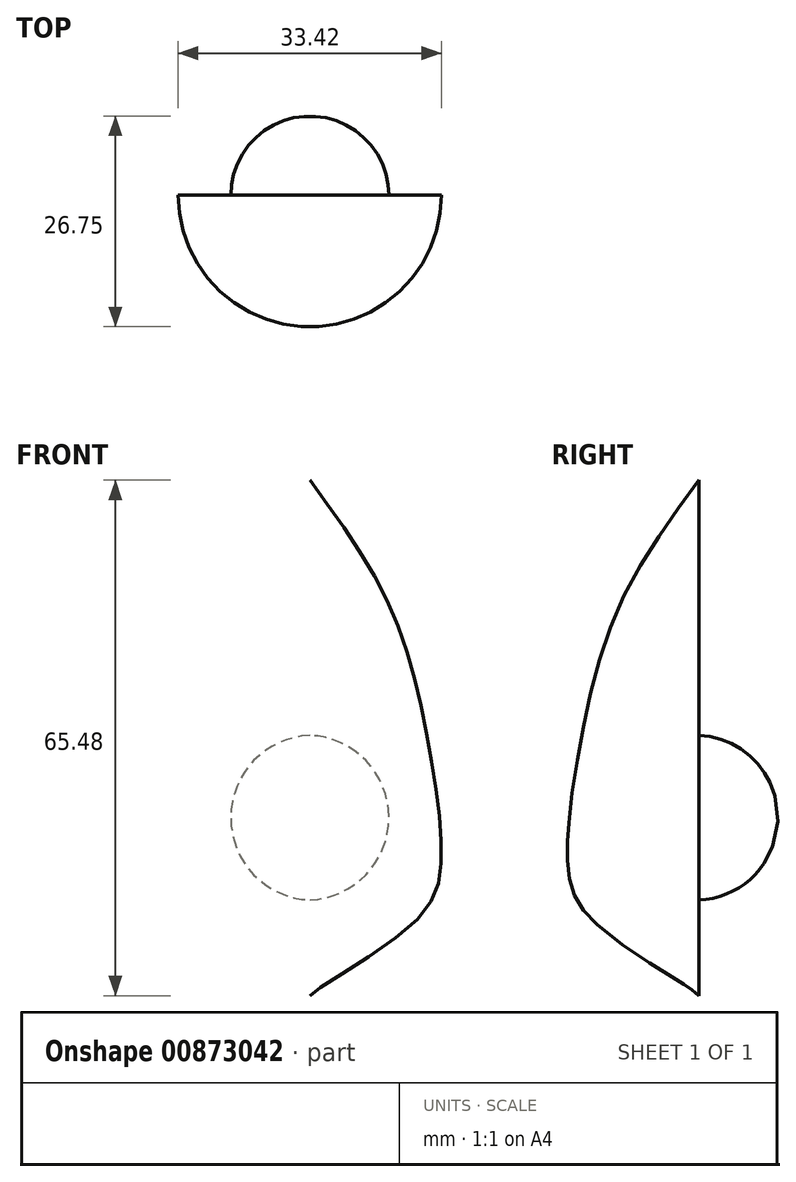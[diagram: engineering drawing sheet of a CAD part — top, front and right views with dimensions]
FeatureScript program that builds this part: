
annotation { "Feature Type Name" : "Feature", "Feature Type Description" : "" }
export const myFeature = defineFeature(function(context is Context, id is Id, definition is map)
    precondition{}
    {
        {
            var Q0;
            Q0=qCreatedBy(makeId("Front.planeOp"),FACE);
            var sketch = newSketch(context, id + "F0", { "sketchPlane" : qUnion([Q0])});
            skFitSpline(sketch, "E0", {"points": [v(0, 47.82) * mm, v(9.92, 32.33) * mm, v(14.8, 15.76) * mm, v(16.7, 0) * mm, v(12.9, -8.7) * mm, v(0, -17.66) * mm, v(0, -17.93) * mm], "startDerivative": vector(51.75, -70.64) * mm, "endDerivative": vector(5, -8.21) * mm});
            skLineSegment(sketch, "E1", {"start": v(0, 47.82) * mm, "end": v(0, -17.66) * mm});
            skSolve(sketch);
        }
        {
            var Q0;
            {var subQ0=sQuery(id+"F0.wireOp",EDGE,"E1");Q0=makeQuery(id+"F0.imprint","IMPRINT",FACE,{"disambiguationData":[TD([[makeQuery(id+"F0.imprint","IMPRINT",EDGE,{"derivedFrom":subQ0}),1.0]])]});}
            var Q1;
            Q1=sQuery(id+"F0.wireOp",EDGE,"E1");
            revolve(context, id + "F1", {"surfaceOperationType" : NewSurfaceOperationType.NEW, "entities" : qUnion([Q0]), "axis" : qUnion([Q1]), "revolveType" : RevolveType.ONE_DIRECTION, "angle" : 180 * degree});
        }
        {
            var Q0;
            Q0=qCreatedBy(makeId("Front.planeOp"),FACE);
            var sketch = newSketch(context, id + "F2", { "sketchPlane" : qUnion([Q0])});
            skLineSegment(sketch, "E2", {"start": v(0, 15.4) * mm, "end": v(0, -5.5) * mm});
            skArc(sketch, "E3", {"start": v(0, 15.4) * mm, "mid": v(-10.04, 4.95) * mm, "end": v(0, -5.5) * mm});
            skSolve(sketch);
        }
        {
            var Q0;
            Q0=makeQuery(id+"F2.imprint","IMPRINT",FACE,{"disambiguationData":[TD([[makeQuery(id+"F2.imprint","IMPRINT",EDGE,{"derivedFrom":sQuery(id+"F2.wireOp",EDGE,"E2")}),-1.0]])]});
            var Q1;
            Q1=sQuery(id+"F2.wireOp",EDGE,"E2");
            revolve(context, id + "F3", {"operationType" : NewBodyOperationType.ADD, "surfaceOperationType" : NewSurfaceOperationType.NEW, "entities" : qUnion([Q0]), "axis" : qUnion([Q1]), "revolveType" : RevolveType.FULL});
        }
    });
